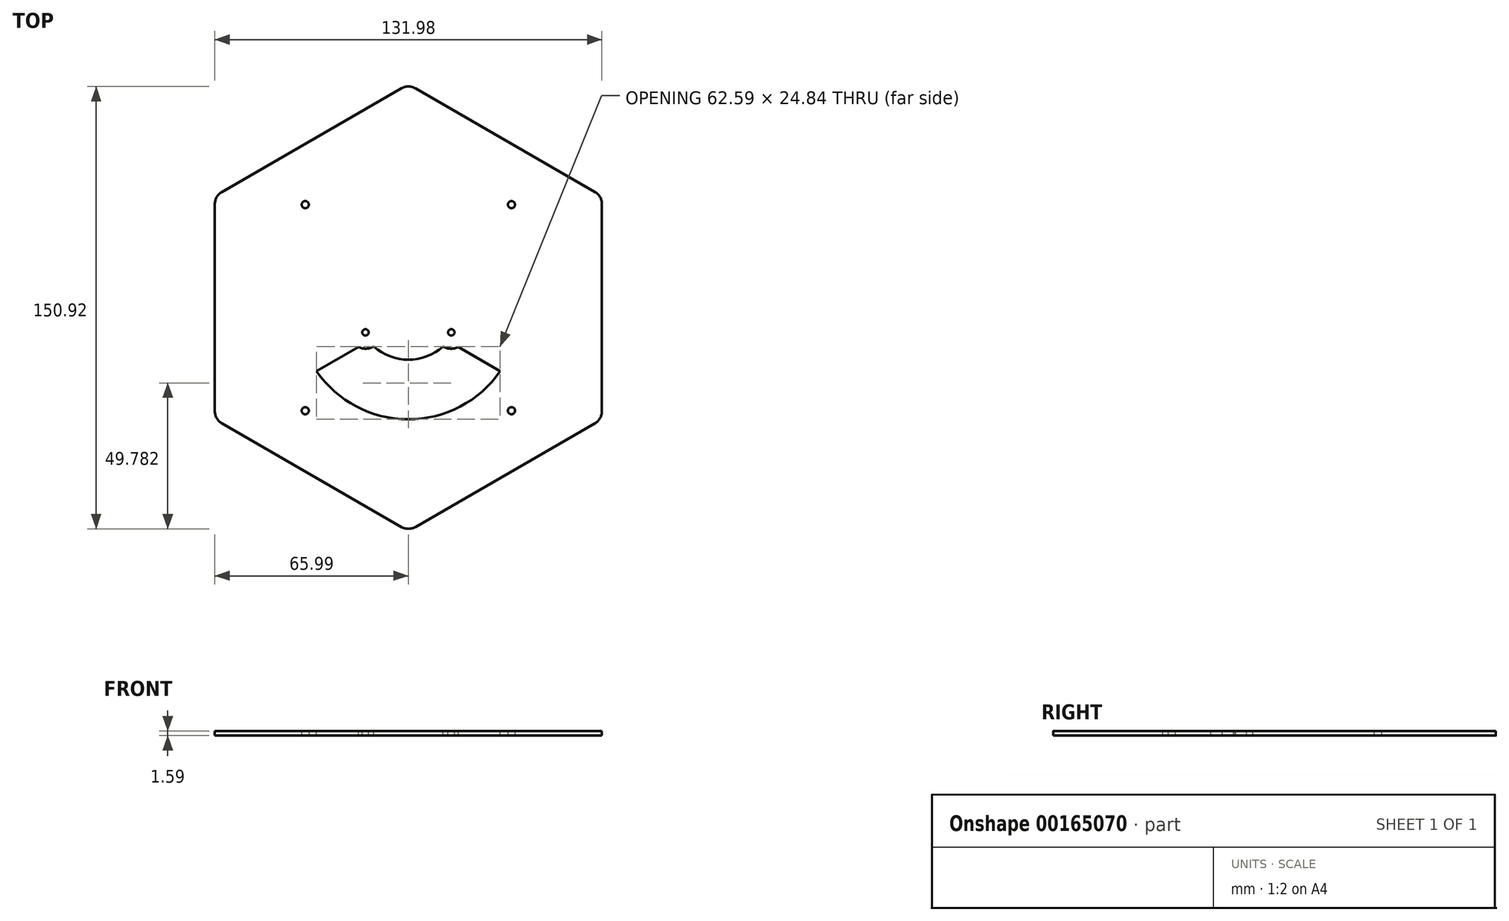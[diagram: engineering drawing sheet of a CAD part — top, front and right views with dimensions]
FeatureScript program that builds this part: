
annotation { "Feature Type Name" : "Feature", "Feature Type Description" : "" }
export const myFeature = defineFeature(function(context is Context, id is Id, definition is map)
    precondition{}
    {
        {
            var Q0;
            Q0=qCreatedBy(makeId("Top.planeOp"),FACE);
            var sketch = newSketch(context, id + "F0", { "sketchPlane" : qUnion([Q0])});
            skLineSegment(sketch, "E0.bottom", {"start": v(35.15, -35.15) * mm, "end": v(35.15, 35.15) * mm, "construction": true});
            skLineSegment(sketch, "E0.top", {"start": v(-35.15, -35.15) * mm, "end": v(-35.15, 35.15) * mm, "construction": true});
            skLineSegment(sketch, "E0.left", {"start": v(35.15, -35.15) * mm, "end": v(-35.15, -35.15) * mm, "construction": true});
            skLineSegment(sketch, "E0.right", {"start": v(35.15, 35.15) * mm, "end": v(-35.15, 35.15) * mm, "construction": true});
            skPoint(sketch, "E0.middle", {"position": v(0, 0) * mm});
            skCircle(sketch, "E1", {"center": v(0, 0) * mm, "radius": 38.1 * mm, "construction": true});
            skCircle(sketch, "E2", {"center": v(35.15, -35.15) * mm, "radius": 1.22 * mm});
            skCircle(sketch, "E3", {"center": v(35.15, 35.15) * mm, "radius": 1.22 * mm});
            skCircle(sketch, "E4", {"center": v(-35.15, 35.15) * mm, "radius": 1.22 * mm});
            skCircle(sketch, "E5", {"center": v(-35.15, -35.15) * mm, "radius": 1.22 * mm});
            skCircle(sketch, "E6", {"center": v(35.15, -35.15) * mm, "radius": 4.53 * mm, "construction": true});
            skCircle(sketch, "E7.cCircle", {"center": v(0, 0) * mm, "radius": 66 * mm, "construction": true});
            skLineSegment(sketch, "E7.0", {"start": v(66, 38.1) * mm, "end": v(66, -38.1) * mm});
            skLineSegment(sketch, "E7.1", {"start": v(66, -38.1) * mm, "end": v(0, -76.2) * mm});
            skLineSegment(sketch, "E7.2", {"start": v(0, -76.2) * mm, "end": v(-66, -38.1) * mm});
            skLineSegment(sketch, "E7.3", {"start": v(-66, -38.1) * mm, "end": v(-66, 38.1) * mm});
            skLineSegment(sketch, "E7.4", {"start": v(-66, 38.1) * mm, "end": v(0, 76.2) * mm});
            skLineSegment(sketch, "E7.5", {"start": v(0, 76.2) * mm, "end": v(66, 38.1) * mm});
            skPoint(sketch, "E7.0.midPoint", {"position": v(66, 0) * mm});
            skCircle(sketch, "E8.cCircle", {"center": v(0, 0) * mm, "radius": 52.55 * mm, "construction": true});
            skLineSegment(sketch, "E8.0", {"start": v(52.55, 30.34) * mm, "end": v(52.55, -30.34) * mm, "construction": true});
            skLineSegment(sketch, "E8.1", {"start": v(52.55, -30.34) * mm, "end": v(0, -60.68) * mm, "construction": true});
            skLineSegment(sketch, "E8.2", {"start": v(0, -60.68) * mm, "end": v(-52.55, -30.34) * mm, "construction": true});
            skLineSegment(sketch, "E8.3", {"start": v(-52.55, -30.34) * mm, "end": v(-52.55, 30.34) * mm, "construction": true});
            skLineSegment(sketch, "E8.4", {"start": v(-52.55, 30.34) * mm, "end": v(0, 60.68) * mm, "construction": true});
            skLineSegment(sketch, "E8.5", {"start": v(0, 60.68) * mm, "end": v(52.55, 30.34) * mm, "construction": true});
            skPoint(sketch, "E8.0.midPoint", {"position": v(52.55, 0) * mm});
            skSolve(sketch);
        }
        {
            var Q0;
            Q0=makeQuery(id+"F0.imprint","IMPRINT",FACE,{"disambiguationData":[TD([[makeQuery(id+"F0.imprint","IMPRINT",EDGE,{"derivedFrom":sQuery(id+"F0.wireOp",EDGE,"E1")}),-1.0]])]});
            var Q1;
            Q1=makeQuery(id+"F0.imprint","IMPRINT",FACE,{"disambiguationData":[TD([[makeQuery(id+"F0.imprint","IMPRINT",EDGE,{"derivedFrom":sQuery(id+"F0.wireOp",EDGE,"E2")}),-1.0]])]});
            extrude(context, id + "F1", {"entities" : qUnion([Q0, Q1]), "depth" : 1.59 * mm});
        }
        {
            var Q0;
            Q0=makeQuery(id+"F1.opExtrude","CAP_FACE",FACE,{"disambiguationData":[OSD([sQuery(id+"F0.wireOp",EDGE,"E2"),sQuery(id+"F0.wireOp",EDGE,"E3"),sQuery(id+"F0.wireOp",EDGE,"E4"),sQuery(id+"F0.wireOp",EDGE,"E5"),sQuery(id+"F0.wireOp",EDGE,"R1JFTZ4v-WKVF-8XfW-xGAy-tLIKOYTsBxTY.bottom"),sQuery(id+"F0.wireOp",EDGE,"R1JFTZ4v-WKVF-8XfW-xGAy-tLIKOYTsBxTY.top"),sQuery(id+"F0.wireOp",EDGE,"R1JFTZ4v-WKVF-8XfW-xGAy-tLIKOYTsBxTY.left"),sQuery(id+"F0.wireOp",EDGE,"R1JFTZ4v-WKVF-8XfW-xGAy-tLIKOYTsBxTY.right")])],"isStart":false});
            var sketch = newSketch(context, id + "F2", { "sketchPlane" : qUnion([Q0])});
            skArc(sketch, "E9", {"start": v(-11.85, -13.26) * mm, "mid": v(0, -17.78) * mm, "end": v(11.85, -13.26) * mm});
            skArc(sketch, "E10", {"start": v(-31.3, -21.73) * mm, "mid": v(0, -38.1) * mm, "end": v(31.3, -21.73) * mm});
            skLineSegment(sketch, "E11", {"start": v(0, -17.78) * mm, "end": v(0, 0) * mm, "construction": true});
            skArc(sketch, "E12", {"start": v(11.85, -13.26) * mm, "mid": v(14.4, -14) * mm, "end": v(16.99, -13.47) * mm});
            skLineSegment(sketch, "E13", {"start": v(11.85, -13.26) * mm, "end": v(14.63, -8.44) * mm, "construction": true});
            skCircle(sketch, "E14", {"center": v(14.63, -8.44) * mm, "radius": 1.1 * mm});
            skLineSegment(sketch, "E15", {"start": v(16.99, -13.47) * mm, "end": v(31.3, -21.73) * mm});
            skLineSegment(sketch, "E16", {"start": v(0, 0) * mm, "end": v(14.63, -8.44) * mm, "construction": true});
            skLineSegment(sketch, "E17", {"start": v(14.63, -8.44) * mm, "end": v(25.73, -14.85) * mm, "construction": true});
            skLineSegment(sketch, "E18", {"start": v(25.73, -14.85) * mm, "end": v(24.14, -17.6) * mm, "construction": true});
            skLineSegment(sketch, "E19", {"start": v(-11.85, -13.26) * mm, "end": v(-14.63, -8.44) * mm, "construction": true});
            skLineSegment(sketch, "E20", {"start": v(-31.3, -21.73) * mm, "end": v(-16.99, -13.47) * mm});
            skArc(sketch, "E21", {"start": v(-16.99, -13.47) * mm, "mid": v(-14.4, -14) * mm, "end": v(-11.85, -13.26) * mm});
            skCircle(sketch, "E22", {"center": v(-14.63, -8.44) * mm, "radius": 1.1 * mm});
            skLineSegment(sketch, "E23", {"start": v(0, 0) * mm, "end": v(-14.63, -8.44) * mm, "construction": true});
            skLineSegment(sketch, "E24", {"start": v(-14.63, -8.44) * mm, "end": v(-25.73, -14.85) * mm, "construction": true});
            skLineSegment(sketch, "E25", {"start": v(-25.73, -14.85) * mm, "end": v(-24.14, -17.6) * mm, "construction": true});
            skSolve(sketch);
        }
        {
            var Q0;
            Q0 = qSketchRegion(id + "F2", true);
            var Q1;
            Q1=makeQuery(id+"F1.opExtrude","CAP_FACE",FACE,{"disambiguationData":[OSD([sQuery(id+"F0.wireOp",EDGE,"E2"),sQuery(id+"F0.wireOp",EDGE,"E3"),sQuery(id+"F0.wireOp",EDGE,"E4"),sQuery(id+"F0.wireOp",EDGE,"E5"),sQuery(id+"F0.wireOp",EDGE,"R1JFTZ4v-WKVF-8XfW-xGAy-tLIKOYTsBxTY.bottom"),sQuery(id+"F0.wireOp",EDGE,"R1JFTZ4v-WKVF-8XfW-xGAy-tLIKOYTsBxTY.top"),sQuery(id+"F0.wireOp",EDGE,"R1JFTZ4v-WKVF-8XfW-xGAy-tLIKOYTsBxTY.left"),sQuery(id+"F0.wireOp",EDGE,"R1JFTZ4v-WKVF-8XfW-xGAy-tLIKOYTsBxTY.right")])],"isStart":true});
            extrude(context, id + "F3", {"entities" : qUnion([Q0]), "operationType" : NewBodyOperationType.REMOVE, "endBound" : BoundingType.UP_TO_SURFACE, "oppositeDirection" : true, "endBoundEntityFace" : qUnion([Q1]), "depth" : 25.4 * mm});
        }
        {
            var Q0;
            Q0=makeQuery(id+"F1.opExtrude","SWEPT_EDGE",EDGE,{"disambiguationData":[OSD([sQuery(id+"F0.wireOp",EDGE,"E7.3"),sQuery(id+"F0.wireOp",EDGE,"E7.4")])]});
            var Q1;
            Q1=makeQuery(id+"F1.opExtrude","SWEPT_EDGE",EDGE,{"disambiguationData":[OSD([sQuery(id+"F0.wireOp",EDGE,"E7.4"),sQuery(id+"F0.wireOp",EDGE,"E7.5")])]});
            var Q2;
            Q2=makeQuery(id+"F1.opExtrude","SWEPT_EDGE",EDGE,{"disambiguationData":[OSD([sQuery(id+"F0.wireOp",EDGE,"E7.0"),sQuery(id+"F0.wireOp",EDGE,"E7.5")])]});
            var Q3;
            Q3=makeQuery(id+"F1.opExtrude","SWEPT_EDGE",EDGE,{"disambiguationData":[OSD([sQuery(id+"F0.wireOp",EDGE,"E7.0"),sQuery(id+"F0.wireOp",EDGE,"E7.1")])]});
            var Q4;
            Q4=makeQuery(id+"F1.opExtrude","SWEPT_EDGE",EDGE,{"disambiguationData":[OSD([sQuery(id+"F0.wireOp",EDGE,"E7.1"),sQuery(id+"F0.wireOp",EDGE,"E7.2")])]});
            var Q5;
            Q5=makeQuery(id+"F1.opExtrude","SWEPT_EDGE",EDGE,{"disambiguationData":[OSD([sQuery(id+"F0.wireOp",EDGE,"E7.2"),sQuery(id+"F0.wireOp",EDGE,"E7.3")])]});
            fillet(context, id + "F4", {"entities" : qUnion([Q0, Q1, Q2, Q3, Q4, Q5]), "radius" : 4.76 * mm, "tangentPropagation" : true, "allowEdgeOverflow" : false});
        }
    });
